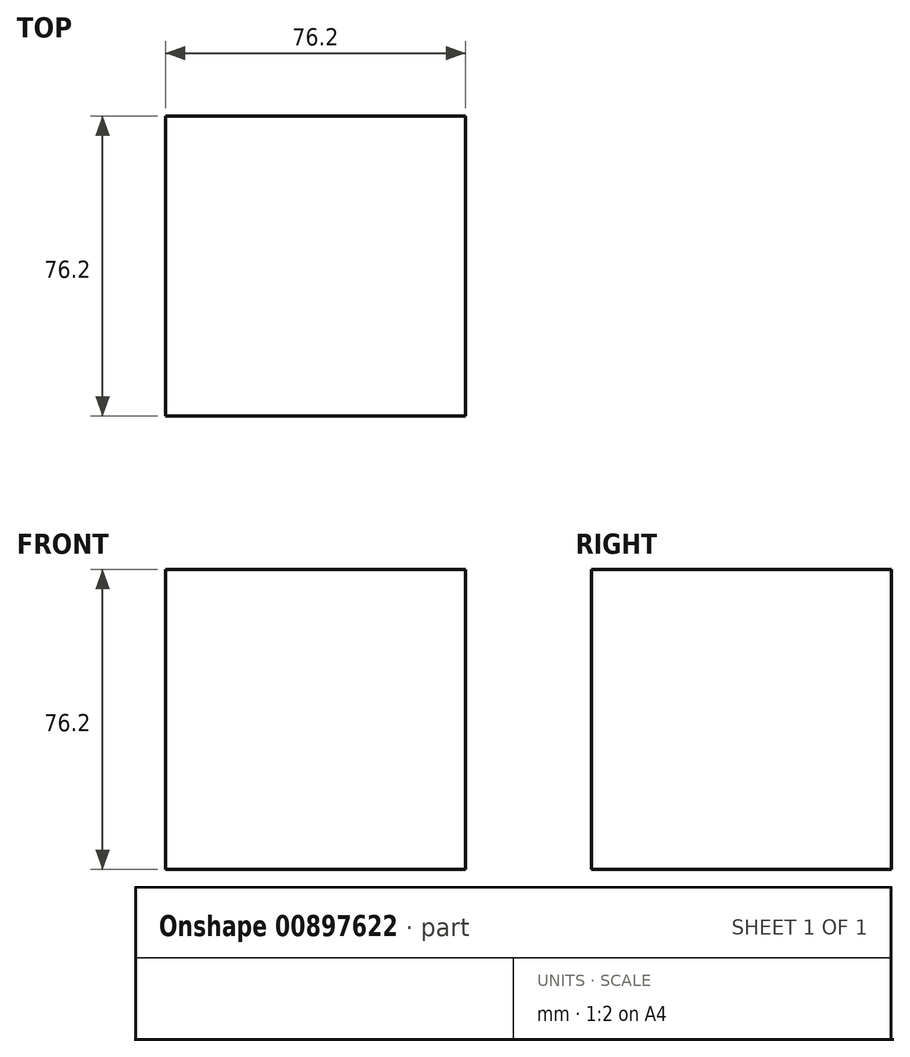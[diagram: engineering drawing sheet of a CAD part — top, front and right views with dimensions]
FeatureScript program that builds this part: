
annotation { "Feature Type Name" : "Feature", "Feature Type Description" : "" }
export const myFeature = defineFeature(function(context is Context, id is Id, definition is map)
    precondition{}
    {
        {
            var Q0;
            Q0=qCreatedBy(makeId("Front.planeOp"),FACE);
            var sketch = newSketch(context, id + "F0", { "sketchPlane" : qUnion([Q0])});
            skLineSegment(sketch, "E0.bottom", {"start": v(-38.1, 38.1) * mm, "end": v(38.1, 38.1) * mm});
            skLineSegment(sketch, "E0.top", {"start": v(-38.1, -38.1) * mm, "end": v(38.1, -38.1) * mm});
            skLineSegment(sketch, "E0.left", {"start": v(-38.1, 38.1) * mm, "end": v(-38.1, -38.1) * mm});
            skLineSegment(sketch, "E0.right", {"start": v(38.1, 38.1) * mm, "end": v(38.1, -38.1) * mm});
            skPoint(sketch, "E0.middle", {"position": v(0, 0) * mm});
            skSolve(sketch);
        }
        {
            var Q0;
            Q0 = qSketchRegion(id + "F0", true);
            extrude(context, id + "F1", {"entities" : qUnion([Q0]), "depth" : 76.2 * mm, "offsetDistance" : 25.4 * mm});
        }
    });
